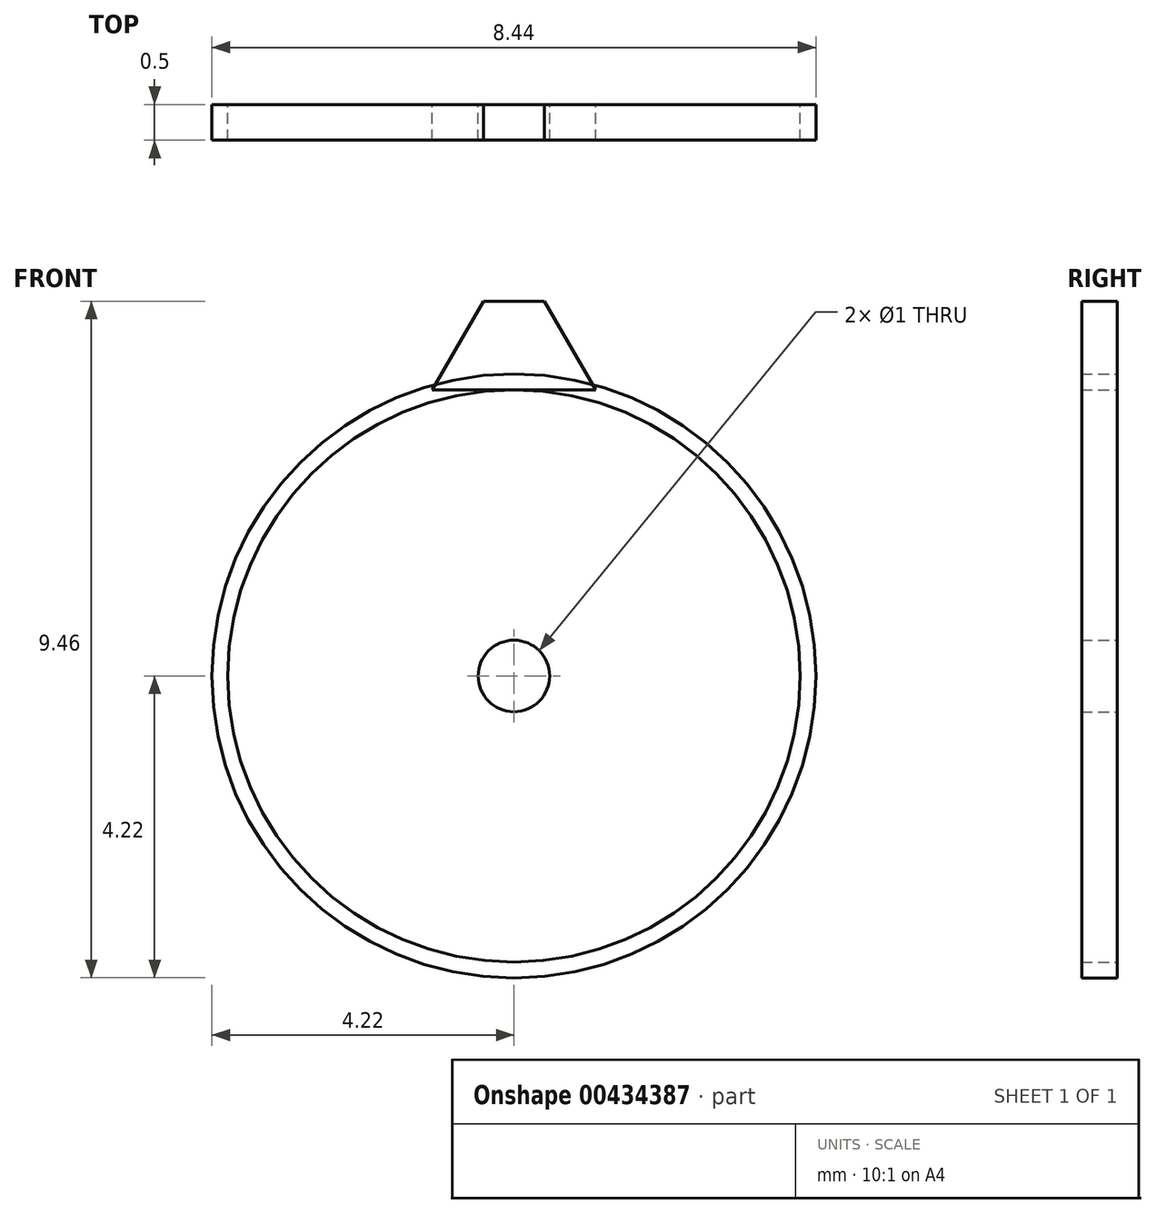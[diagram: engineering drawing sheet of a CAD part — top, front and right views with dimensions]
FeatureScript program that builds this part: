
annotation { "Feature Type Name" : "Feature", "Feature Type Description" : "" }
export const myFeature = defineFeature(function(context is Context, id is Id, definition is map)
    precondition{}
    {
        {
            var Q0;
            Q0=qCreatedBy(makeId("Front.planeOp"),FACE);
            var sketch = newSketch(context, id + "F0", { "sketchPlane" : qUnion([Q0])});
            skCircle(sketch, "E0", {"center": v(0, 0) * mm, "radius": 4 * mm});
            skSolve(sketch);
        }
        {
            var Q0;
            Q0 = qSketchRegion(id + "F0", true);
            extrude(context, id + "F1", {"entities" : qUnion([Q0]), "depth" : 0.5 * mm});
        }
        {
            var Q0;
            Q0=qCreatedBy(makeId("Front.planeOp"),FACE);
            var sketch = newSketch(context, id + "F2", { "sketchPlane" : qUnion([Q0])});
            skLineSegment(sketch, "E1", {"start": v(0, 4) * mm, "end": v(0, 4) * mm});
            skLineSegment(sketch, "E2", {"start": v(0, 4) * mm, "end": v(1.14, 4) * mm});
            skLineSegment(sketch, "E3", {"start": v(0, 4) * mm, "end": v(-1.14, 4) * mm});
            skLineSegment(sketch, "E4", {"start": v(0, 4) * mm, "end": v(0, 5.24) * mm});
            skLineSegment(sketch, "E5", {"start": v(0, 5.24) * mm, "end": v(-0.43, 5.24) * mm});
            skLineSegment(sketch, "E6", {"start": v(0, 5.24) * mm, "end": v(0.43, 5.24) * mm});
            skLineSegment(sketch, "E7", {"start": v(-0.43, 5.24) * mm, "end": v(-1.14, 4) * mm});
            skLineSegment(sketch, "E8", {"start": v(0.43, 5.24) * mm, "end": v(1.14, 4) * mm});
            skSolve(sketch);
        }
        {
            var Q0;
            Q0 = qSketchRegion(id + "F2", true);
            extrude(context, id + "F3", {"entities" : qUnion([Q0]), "depth" : 0.5 * mm});
        }
        {
            var Q0;
            Q0=qCreatedBy(makeId("Front.planeOp"),FACE);
            var sketch = newSketch(context, id + "F4", { "sketchPlane" : qUnion([Q0])});
            skCircle(sketch, "E9", {"center": v(0, 0) * mm, "radius": 4.22 * mm});
            skSolve(sketch);
        }
        {
            var Q0;
            Q0 = qSketchRegion(id + "F4", true);
            extrude(context, id + "F5", {"entities" : qUnion([Q0]), "depth" : 0.5 * mm});
        }
        {
            var Q0;
            Q0=qCreatedBy(makeId("Front.planeOp"),FACE);
            var sketch = newSketch(context, id + "F6", { "sketchPlane" : qUnion([Q0])});
            skCircle(sketch, "E10", {"center": v(0, 0) * mm, "radius": 0.5 * mm});
            skSolve(sketch);
        }
        {
            var Q0;
            Q0 = qSketchRegion(id + "F6", true);
            extrude(context, id + "F7", {"entities" : qUnion([Q0]), "operationType" : NewBodyOperationType.REMOVE, "oppositeDirection" : true, "depth" : -0.5 * mm});
        }
    });
